# Revit family: 1
name_source: partatom
category: Generic Models
revit_build: Autodesk Revit 2018 (Build: 20190510_1515(x64)
units: mm (PartAtom-declared; Revit-internal decimal feet)

## family parameters
Can host rebar = No
Cut with Voids When Loaded = No
Host = Face
OmniClass Number = 23.19.31.17
OmniClass Title = Sanitary Room Units
Part Type = Normal
Room Calculation Point = No
Round Connector Dimension = Use Diameter
Shared = No

## types (2) — shared parameters
BIMobject category = Accessories
Default Elevation = 1219 mm
Design country = Germany
ETIM classification = EC010555 | Lavatory brush set
IFC Classification = Furnishing Element
Installation instructions = https://pro.duravit.com
Manufacturer = Duravit
Manufacturer country = Germany
Manufacturer name = DURAVIT AG
Masterformat 2014 Code = 01 52 19
Masterformat 2014 Description = Sanitary Facilities
Material main = Chrome
Model = Starck T Brush set 80x118x435 mm - 009946
OmniClass Code = 23-19 31 17
OmniClass Description = Sanitary Room Units
Product Guid = b7d15c25-0851-4432-bb26-d7f97d5956ec
Product SKU = Starck-T-Brush-set-80x118x435-mm-009946
Product certification = https://pro.duravit.com
Product data url = https://bimobject.com
Product family = Starck T
Product group = Toilet accessories
Product name = Starck T Brush set 80x118x435 mm - 009946
Product url = https://pro.duravit.com
QR code = https://bimobject.com
Technical description = https://pro.duravit.com
UNSPSC Code = 301815
URL = https://www.duravit.com
Uniclass 2015 Code = Pr_40_20
Uniclass 2015 Name = Sanitary fittings and accessories
Uniformat II Code = D2010
Uniformat II Description = Plumbing Fixtures
Weight Net (Kg) = 1,1
Youtube clip = https://pro.duravit.com
zero-valued in all types: Edition number

## per-type parameters (varying)
| type | Description | Main material |
| 46 - Black Matt | Duravit Starck T Brush set Chrome 80x118x435 mm - 0099461000 | Duravit - Metal - 46 - Black Matt |
| 10 - Chrome | Duravit Starck T Brush set Black Matt 80x118x435 mm - 0099464600 | Duravit - Metal - 10 - Chrome |

## geometry (parser evidence)
native form markers: Sweep x3
no freeform markers — native parametric forms only
